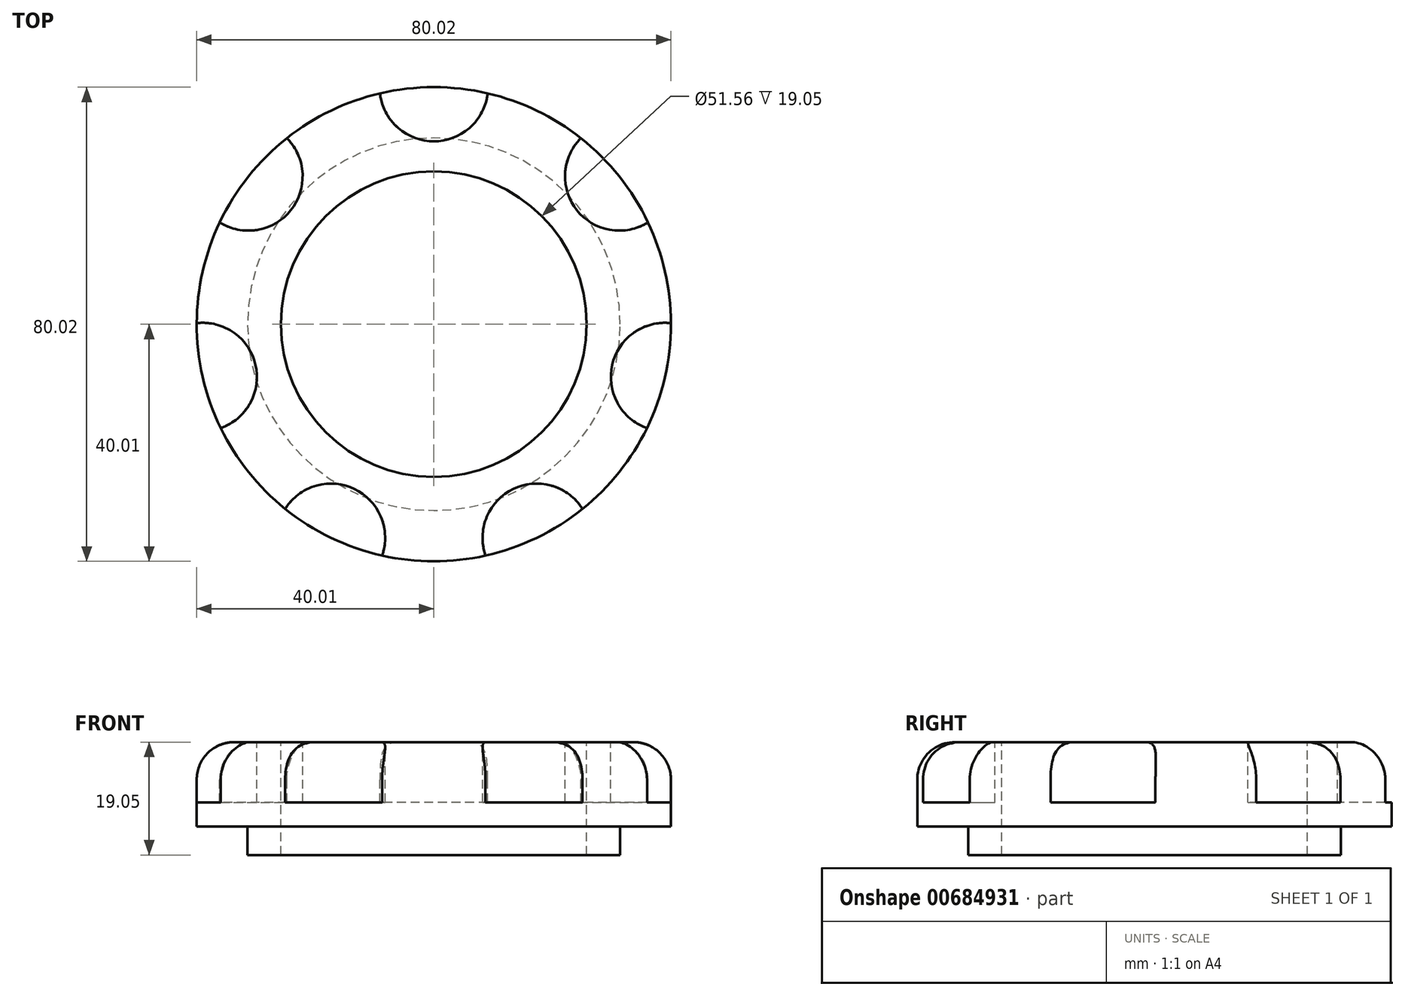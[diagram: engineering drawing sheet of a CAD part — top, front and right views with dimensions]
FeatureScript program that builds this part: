
annotation { "Feature Type Name" : "Feature", "Feature Type Description" : "" }
export const myFeature = defineFeature(function(context is Context, id is Id, definition is map)
    precondition{}
    {
        {
            var Q0;
            Q0=qCreatedBy(makeId("Front.planeOp"),FACE);
            var sketch = newSketch(context, id + "F0", { "sketchPlane" : qUnion([Q0])});
            skLineSegment(sketch, "E0", {"start": v(0, 56.07) * mm, "end": v(0, -45.26) * mm, "construction": true});
            skLineSegment(sketch, "E1", {"start": v(25.78, 0) * mm, "end": v(25.78, 19.05) * mm});
            skLineSegment(sketch, "E2", {"start": v(25.78, 19.05) * mm, "end": v(33.66, 19.05) * mm});
            skLineSegment(sketch, "E3", {"start": v(40, 12.7) * mm, "end": v(40, 4.83) * mm});
            skLineSegment(sketch, "E4", {"start": v(40, 4.83) * mm, "end": v(31.43, 4.83) * mm});
            skLineSegment(sketch, "E5", {"start": v(31.43, 4.83) * mm, "end": v(31.43, 0) * mm});
            skLineSegment(sketch, "E6", {"start": v(31.43, 0) * mm, "end": v(25.78, 0) * mm});
            skLineSegment(sketch, "E7", {"start": v(-19.63, 0) * mm, "end": v(12.27, 0) * mm, "construction": true});
            skPoint(sketch, "E8.visualSharp", {"position": v(40, 19.05) * mm});
            skArc(sketch, "E8.filletArc", {"start": v(40, 12.7) * mm, "mid": v(38.15, 17.2) * mm, "end": v(33.66, 19.05) * mm});
            skSolve(sketch);
        }
        {
            var Q0;
            Q0 = qSketchRegion(id + "F0", true);
            var Q1;
            Q1=sQuery(id+"F0.wireOp",EDGE,"E0");
            revolve(context, id + "F1", {"surfaceOperationType" : NewSurfaceOperationType.NEW, "entities" : qUnion([Q0]), "axis" : qUnion([Q1]), "revolveType" : RevolveType.FULL});
        }
        {
            var Q0;
            Q0=qCreatedBy(makeId("Top.planeOp"),FACE);
            cPlane(context, id + "F2", {"entities" : qUnion([Q0]), "cplaneType" : CPlaneType.OFFSET, "offset" : 19.05 * mm, "width" : 152.4 * mm, "height" : 152.4 * mm});
        }
        {
            var Q0;
            Q0=qCreatedBy(id+"F2.planeOp",FACE);
            var sketch = newSketch(context, id + "F3", { "sketchPlane" : qUnion([Q0])});
            skLineSegment(sketch, "E9", {"start": v(0, 0) * mm, "end": v(0, 42.16) * mm, "construction": true});
            skLineSegment(sketch, "E10", {"start": v(0, 0) * mm, "end": v(-43.11, 0) * mm, "construction": true});
            skArc(sketch, "E11", {"start": v(-9.08, 38.96) * mm, "mid": v(0, 30.86) * mm, "end": v(9.08, 38.96) * mm});
            skArc(sketch, "E12", {"start": v(9.08, 38.96) * mm, "mid": v(0, 40) * mm, "end": v(-9.08, 38.96) * mm});
            skArc(sketch, "E13.1.0", {"start": v(-24.8, 31.4) * mm, "mid": v(-31.28, 24.94) * mm, "end": v(-36.12, 17.19) * mm});
            skArc(sketch, "E13.1.1", {"start": v(-36.12, 17.19) * mm, "mid": v(-24.13, 19.24) * mm, "end": v(-24.8, 31.4) * mm});
            skArc(sketch, "E13.2.0", {"start": v(-40, 0.19) * mm, "mid": v(-39, -8.9) * mm, "end": v(-35.96, -17.53) * mm});
            skArc(sketch, "E13.2.1", {"start": v(-35.96, -17.53) * mm, "mid": v(-30.09, -6.87) * mm, "end": v(-40, 0.19) * mm});
            skArc(sketch, "E13.3.0", {"start": v(-25.09, -31.16) * mm, "mid": v(-17.36, -36.04) * mm, "end": v(-8.72, -39.04) * mm});
            skArc(sketch, "E13.3.1", {"start": v(-8.72, -39.04) * mm, "mid": v(-13.4, -27.8) * mm, "end": v(-25.09, -31.16) * mm});
            skArc(sketch, "E13.4.0", {"start": v(8.72, -39.04) * mm, "mid": v(17.36, -36.04) * mm, "end": v(25.09, -31.16) * mm});
            skArc(sketch, "E13.4.1", {"start": v(25.09, -31.16) * mm, "mid": v(13.4, -27.8) * mm, "end": v(8.72, -39.04) * mm});
            skArc(sketch, "E13.5.0", {"start": v(35.96, -17.53) * mm, "mid": v(39, -8.9) * mm, "end": v(40, 0.19) * mm});
            skArc(sketch, "E13.5.1", {"start": v(40, 0.19) * mm, "mid": v(30.09, -6.87) * mm, "end": v(35.96, -17.53) * mm});
            skArc(sketch, "E13.6.0", {"start": v(36.12, 17.19) * mm, "mid": v(31.28, 24.94) * mm, "end": v(24.8, 31.4) * mm});
            skArc(sketch, "E13.6.1", {"start": v(24.8, 31.4) * mm, "mid": v(24.13, 19.24) * mm, "end": v(36.12, 17.19) * mm});
            skSolve(sketch);
        }
        {
            var Q0;
            Q0 = qSketchRegion(id + "F3", true);
            extrude(context, id + "F4", {"entities" : qUnion([Q0]), "operationType" : NewBodyOperationType.REMOVE, "oppositeDirection" : true, "depth" : 10.16 * mm, "offsetDistance" : 25.4 * mm});
        }
    });
